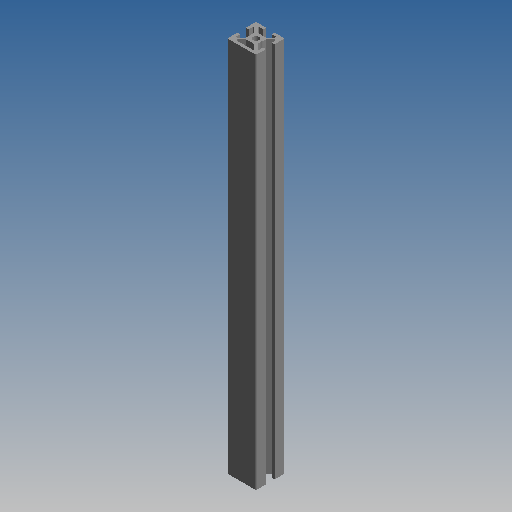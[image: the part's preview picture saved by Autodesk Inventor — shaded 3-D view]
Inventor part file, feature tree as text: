
AUTODESK INVENTOR PART (.ipt)
format: ipt  version: 2020 (Build 240168000, 168)  size: 204,288 bytes
history: native  units: mm (DEFAULTED — no unit token found)
features: other x7, sketch x2, extrude x1, hole x1
ambient origin geometry x8: Origin, YZ Plane, XZ Plane, XY Plane, X Axis, Y Axis, Z Axis, Center Point
bodies: Solid1 (feature_tree)
feature tree (11):
  extrude  "Extrusion1"  TaperAngle=0.0deg  [1 undecoded]
  hole  "Hole1"  [1 undecoded]
  other  "C1_XY"
  other  "C1_YZ"
  other  "C1_ZX"
  other  "C1_X"
  other  "C1_Y"
  other  "C1_Z"
  other  "C1_Center"
  sketch  "Sketch_76"  dims[d2=4.2mm d3=6.0mm d4=4.0mm d5=2.0mm d6=90.0deg d7=263.5mm d8=0.0mm d9=0.0mm]
  sketch  "Sketch2"  dims[d0=263.5mm d1=0.0mm]
note: 2 required parameter values undecoded (feature->parameter linkage not recoverable at this tier; creation-order binding heuristic only, values carry confidence <= 0.55)
